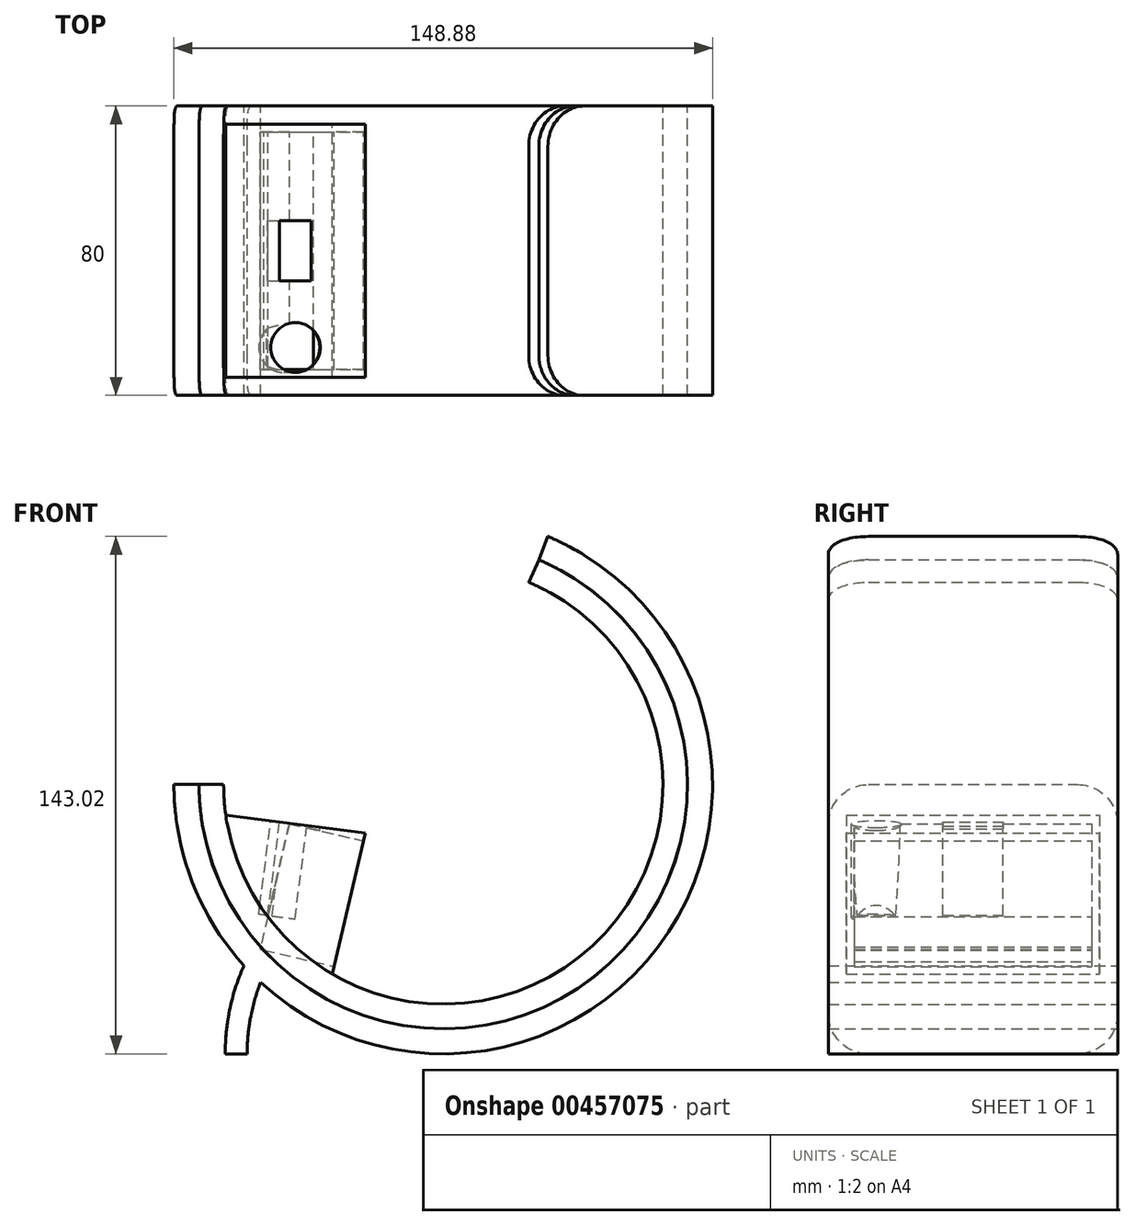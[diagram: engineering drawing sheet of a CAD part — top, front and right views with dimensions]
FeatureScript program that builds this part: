
annotation { "Feature Type Name" : "Feature", "Feature Type Description" : "" }
export const myFeature = defineFeature(function(context is Context, id is Id, definition is map)
    precondition{}
    {
        {
            var Q0;
            Q0=qCreatedBy(makeId("Front.planeOp"),FACE);
            var sketch = newSketch(context, id + "F0", { "sketchPlane" : qUnion([Q0])});
            skArc(sketch, "E0", {"start": v(23.62, 55.93) * mm, "mid": v(33.56, -50.6) * mm, "end": v(-60.71, 0) * mm});
            skArc(sketch, "E1", {"start": v(28.95, 68.58) * mm, "mid": v(41.15, -62.04) * mm, "end": v(-74.44, 0) * mm});
            skArc(sketch, "E2", {"start": v(26.42, 62.12) * mm, "mid": v(37.24, -56.3) * mm, "end": v(-67.5, 0) * mm});
            skLineSegment(sketch, "E3", {"start": v(-60.71, 0) * mm, "end": v(-67.5, 0) * mm});
            skLineSegment(sketch, "E4", {"start": v(-74.44, 0) * mm, "end": v(-67.5, 0) * mm});
            skLineSegment(sketch, "E5", {"start": v(0, 0) * mm, "end": v(0, -74.44) * mm});
            skArc(sketch, "E6", {"start": v(-55.1, -50.05) * mm, "mid": v(-58.96, -61.98) * mm, "end": v(-60.26, -74.44) * mm});
            skArc(sketch, "E7", {"start": v(-50.49, -54.7) * mm, "mid": v(-53.27, -64.4) * mm, "end": v(-54.2, -74.44) * mm});
            skArc(sketch, "E8", {"start": v(50.49, -54.7) * mm, "mid": v(53.27, -64.4) * mm, "end": v(54.2, -74.44) * mm});
            skArc(sketch, "E9", {"start": v(55.1, -50.05) * mm, "mid": v(58.96, -61.98) * mm, "end": v(60.26, -74.44) * mm});
            skLineSegment(sketch, "E10", {"start": v(-60.26, -74.44) * mm, "end": v(-54.2, -74.44) * mm});
            skLineSegment(sketch, "E11", {"start": v(54.2, -74.44) * mm, "end": v(60.26, -74.44) * mm});
            skLineSegment(sketch, "E12", {"start": v(28.95, 68.58) * mm, "end": v(26.42, 62.12) * mm});
            skLineSegment(sketch, "E13", {"start": v(26.42, 62.12) * mm, "end": v(23.62, 55.93) * mm});
            skSolve(sketch);
        }
        {
            var Q0;
            {var subQ0=sQuery(id+"F0.wireOp",EDGE,"E3");Q0=makeQuery(id+"F0.imprint","IMPRINT",FACE,{"disambiguationData":[TD([[makeQuery(id+"F0.imprint","IMPRINT",EDGE,{"derivedFrom":subQ0}),1.0]])]});}
            var Q1;
            {var subQ0=sQuery(id+"F0.wireOp",EDGE,"E13");Q1=makeQuery(id+"F0.imprint","IMPRINT",FACE,{"disambiguationData":[TD([[makeQuery(id+"F0.imprint","IMPRINT",EDGE,{"derivedFrom":subQ0}),1.0]])]});}
            extrude(context, id + "F1", {"entities" : qUnion([Q0, Q1]), "depth" : 80 * mm});
        }
        {
            var Q0;
            {var subQ0=sQuery(id+"F0.wireOp",EDGE,"E4");Q0=makeQuery(id+"F0.imprint","IMPRINT",FACE,{"disambiguationData":[TD([[makeQuery(id+"F0.imprint","IMPRINT",EDGE,{"derivedFrom":subQ0}),-1.0]])]});}
            var Q1;
            {var subQ4=sQuery(id+"F0.wireOp",EDGE,"E12");Q1=makeQuery(id+"F0.imprint","IMPRINT",FACE,{"disambiguationData":[TD([[makeQuery(id+"F0.imprint","IMPRINT",EDGE,{"derivedFrom":subQ4}),1.0]])]});}
            var Q2;
            {var subQ0=sQuery(id+"F0.wireOp",EDGE,"E6");Q2=makeQuery(id+"F0.imprint","IMPRINT",FACE,{"disambiguationData":[TD([[makeQuery(id+"F0.imprint","IMPRINT",EDGE,{"derivedFrom":subQ0}),1.0]])]});}
            var Q3;
            {var subQ0=sQuery(id+"F0.wireOp",EDGE,"E8");Q3=makeQuery(id+"F0.imprint","IMPRINT",FACE,{"disambiguationData":[TD([[makeQuery(id+"F0.imprint","IMPRINT",EDGE,{"derivedFrom":subQ0}),1.0]])]});}
            extrude(context, id + "F2", {"entities" : qUnion([Q0, Q1, Q2, Q3]), "depth" : 80 * mm});
        }
        {
            var Q0;
            Q0=makeQuery(id+"F1.opExtrude","CAP_EDGE",EDGE,{"disambiguationData":[OSD([sQuery(id+"F0.wireOp",EDGE,"E3")])],"isStart":false});
            var Q1;
            Q1=makeQuery(id+"F1.opExtrude","CAP_EDGE",EDGE,{"disambiguationData":[OSD([sQuery(id+"F0.wireOp",EDGE,"E3")])],"isStart":true});
            var Q2;
            Q2=makeQuery(id+"F2.opExtrude","CAP_EDGE",EDGE,{"disambiguationData":[OSD([sQuery(id+"F0.wireOp",EDGE,"E4")])],"isStart":false});
            var Q3;
            Q3=makeQuery(id+"F2.opExtrude","CAP_EDGE",EDGE,{"disambiguationData":[OSD([sQuery(id+"F0.wireOp",EDGE,"E4")])],"isStart":true});
            var Q4;
            Q4=makeQuery(id+"F2.opExtrude","CAP_EDGE",EDGE,{"disambiguationData":[OSD([sQuery(id+"F0.wireOp",EDGE,"E12")])],"isStart":false});
            var Q5;
            Q5=makeQuery(id+"F1.opExtrude","CAP_EDGE",EDGE,{"disambiguationData":[OSD([sQuery(id+"F0.wireOp",EDGE,"E13")])],"isStart":false});
            var Q6;
            Q6=makeQuery(id+"F2.opExtrude","CAP_EDGE",EDGE,{"disambiguationData":[OSD([sQuery(id+"F0.wireOp",EDGE,"E12")])],"isStart":true});
            var Q7;
            Q7=makeQuery(id+"F1.opExtrude","CAP_EDGE",EDGE,{"disambiguationData":[OSD([sQuery(id+"F0.wireOp",EDGE,"E13")])],"isStart":true});
            var Q8;
            Q8=makeQuery(id+"F2.opExtrude","CAP_EDGE",EDGE,{"disambiguationData":[OSD([sQuery(id+"F0.wireOp",EDGE,"E10")])],"isStart":false});
            var Q9;
            Q9=makeQuery(id+"F2.opExtrude","CAP_EDGE",EDGE,{"disambiguationData":[OSD([sQuery(id+"F0.wireOp",EDGE,"E10")])],"isStart":true});
            var Q10;
            Q10=makeQuery(id+"F2.opExtrude","CAP_EDGE",EDGE,{"disambiguationData":[OSD([sQuery(id+"F0.wireOp",EDGE,"E11")])],"isStart":false});
            var Q11;
            Q11=makeQuery(id+"F2.opExtrude","CAP_EDGE",EDGE,{"disambiguationData":[OSD([sQuery(id+"F0.wireOp",EDGE,"E11")])],"isStart":true});
            fillet(context, id + "F3", {"entities" : qUnion([Q0, Q1, Q2, Q3, Q4, Q5, Q6, Q7, Q8, Q9, Q10, Q11]), "radius" : 11.1 * mm, "tangentPropagation" : true, "allowEdgeOverflow" : false});
        }
        {
            var Q0;
            Q0=qCreatedBy(makeId("Front.planeOp"),FACE);
            cPlane(context, id + "F4", {"entities" : qUnion([Q0]), "cplaneType" : CPlaneType.OFFSET, "offset" : 40 * mm, "width" : 150 * mm, "height" : 150 * mm});
        }
        {
            var Q0;
            Q0=qCreatedBy(id+"F4.planeOp",FACE);
            var sketch = newSketch(context, id + "F5", { "sketchPlane" : qUnion([Q0])});
            skArc(sketch, "E14", {"start": v(-60.12, -8.49) * mm, "mid": v(-50.41, -33.84) * mm, "end": v(-30.63, -52.42) * mm});
            skCircle(sketch, "E15", {"center": v(0, 0) * mm, "radius": 25.43 * mm, "construction": true});
            skLineSegment(sketch, "E16", {"start": v(-30.63, -52.42) * mm, "end": v(-21.58, -13.45) * mm});
            skLineSegment(sketch, "E17", {"start": v(-60.12, -8.49) * mm, "end": v(-21.58, -13.45) * mm});
            skSolve(sketch);
        }
        {
            var Q0;
            Q0=makeQuery(id+"F5.imprint","IMPRINT",FACE,{"disambiguationData":[TD([[makeQuery(id+"F5.imprint","IMPRINT",EDGE,{"derivedFrom":sQuery(id+"F5.wireOp",EDGE,"E14")}),1.0]])]});
            extrude(context, id + "F6", {"entities" : qUnion([Q0]), "depth" : 35 * mm, "hasSecondDirection" : true, "secondDirectionOppositeDirection" : true, "secondDirectionDepth" : 35 * mm});
        }
        {
            var Q0;
            Q0=makeQuery(id+"F6.opExtrude","SWEPT_FACE",FACE,{"disambiguationData":[OSD([sQuery(id+"F5.wireOp",EDGE,"E17")])]});
            var sketch = newSketch(context, id + "F7", { "sketchPlane" : qUnion([Q0])});
            skPoint(sketch, "E18.0", {"position": v(-39.11, -75) * mm});
            skPoint(sketch, "E19.0", {"position": v(-39.11, -5) * mm});
            skPoint(sketch, "E20.0", {"position": v(-58.54, -40) * mm});
            skPoint(sketch, "E21.0", {"position": v(-19.68, -40) * mm});
            skLineSegment(sketch, "E22", {"start": v(-39.11, -75) * mm, "end": v(-39.11, -5) * mm, "construction": true});
            skLineSegment(sketch, "E23", {"start": v(-19.68, -40) * mm, "end": v(-58.54, -40) * mm, "construction": true});
            skLineSegment(sketch, "E24.bottom", {"start": v(-43.52, -48.34) * mm, "end": v(-34.7, -48.34) * mm});
            skLineSegment(sketch, "E24.top", {"start": v(-43.52, -31.66) * mm, "end": v(-34.7, -31.66) * mm});
            skLineSegment(sketch, "E24.left", {"start": v(-43.52, -48.34) * mm, "end": v(-43.52, -31.66) * mm});
            skLineSegment(sketch, "E24.right", {"start": v(-34.7, -48.34) * mm, "end": v(-34.7, -31.66) * mm});
            skPoint(sketch, "E24.middle", {"position": v(-39.11, -40) * mm});
            skLineSegment(sketch, "E25", {"start": v(-39.11, -75) * mm, "end": v(-58.54, -40) * mm, "construction": true});
            skLineSegment(sketch, "E26", {"start": v(-58.54, -75) * mm, "end": v(-39.11, -40) * mm, "construction": true});
            skLineSegment(sketch, "E27", {"start": v(-48.83, -57.5) * mm, "end": v(-39.11, -57.5) * mm, "construction": true});
            skLineSegment(sketch, "E28", {"start": v(-39.11, -75) * mm, "end": v(-39.11, -66.75) * mm});
            skCircle(sketch, "E29", {"center": v(-39.11, -66.75) * mm, "radius": 6.9 * mm});
            skSolve(sketch);
        }
        {
            var Q0;
            Q0=makeQuery(id+"F7.imprint","IMPRINT",FACE,{"disambiguationData":[TD([[makeQuery(id+"F7.imprint","IMPRINT",EDGE,{"derivedFrom":sQuery(id+"F7.wireOp",EDGE,"E29")}),1.0]])]});
            extrude(context, id + "F8", {"entities" : qUnion([Q0]), "operationType" : NewBodyOperationType.REMOVE, "oppositeDirection" : true, "depth" : 26 * mm});
        }
        {
            var Q0;
            Q0=makeQuery(id+"F7.imprint","IMPRINT",FACE,{"disambiguationData":[TD([[makeQuery(id+"F7.imprint","IMPRINT",EDGE,{"derivedFrom":sQuery(id+"F7.wireOp",EDGE,"E24.bottom")}),1.0]])]});
            extrude(context, id + "F9", {"entities" : qUnion([Q0]), "operationType" : NewBodyOperationType.REMOVE, "oppositeDirection" : true, "depth" : 26 * mm});
        }
        {
            var Q0;
            Q0=makeQuery(id+"F6.opExtrude","SWEPT_FACE",FACE,{"disambiguationData":[OSD([sQuery(id+"F5.wireOp",EDGE,"E16")])]});
            var sketch = newSketch(context, id + "F10", { "sketchPlane" : qUnion([Q0])});
            skPoint(sketch, "E30.0", {"position": v(-40, -58) * mm});
            skPoint(sketch, "E31.0", {"position": v(-40, -17.98) * mm});
            skPoint(sketch, "E32.0", {"position": v(-5, -37.99) * mm});
            skLineSegment(sketch, "E33", {"start": v(-75, -37.99) * mm, "end": v(-5, -37.99) * mm, "construction": true});
            skLineSegment(sketch, "E34", {"start": v(-40, -58) * mm, "end": v(-40, -17.98) * mm, "construction": true});
            skLineSegment(sketch, "E35.bottom", {"start": v(-72.86, -20.17) * mm, "end": v(-7.14, -20.17) * mm});
            skLineSegment(sketch, "E35.top", {"start": v(-72.86, -55.8) * mm, "end": v(-7.14, -55.8) * mm});
            skLineSegment(sketch, "E35.left", {"start": v(-72.86, -20.17) * mm, "end": v(-72.86, -55.8) * mm});
            skLineSegment(sketch, "E35.right", {"start": v(-7.14, -20.17) * mm, "end": v(-7.14, -55.8) * mm});
            skPoint(sketch, "E35.middle", {"position": v(-40, -37.99) * mm});
            skSolve(sketch);
        }
        {
            var Q0;
            Q0=makeQuery(id+"F10.imprint","IMPRINT",FACE,{"disambiguationData":[TD([[makeQuery(id+"F10.imprint","IMPRINT",EDGE,{"derivedFrom":sQuery(id+"F10.wireOp",EDGE,"E35.bottom")}),-1.0]])]});
            extrude(context, id + "F11", {"entities" : qUnion([Q0]), "operationType" : NewBodyOperationType.REMOVE, "oppositeDirection" : true, "depth" : 21 * mm});
        }
    });
